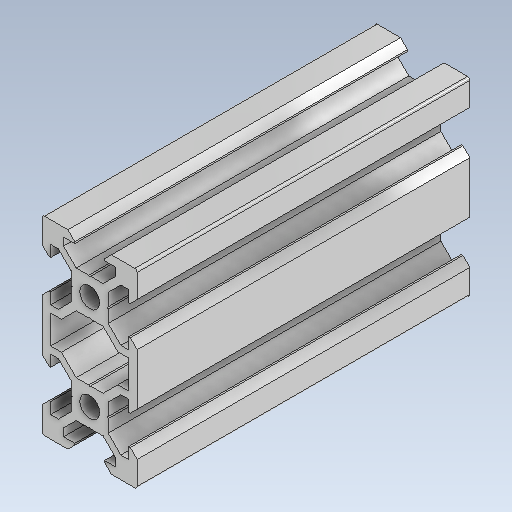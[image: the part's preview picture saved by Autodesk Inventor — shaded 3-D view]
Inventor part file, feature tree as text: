
AUTODESK INVENTOR PART (.ipt)
format: ipt  version: 2020 (Build 240168000, 168)  size: 277,504 bytes
history: native  units: mm
features: extrude x1, sketch x1
ambient origin geometry x8: Origin, YZ Plane, XZ Plane, XY Plane, X Axis, Y Axis, Z Axis, Center Point
bodies: Solid1 (feature_tree)
feature tree (2):
  extrude  "Extrusion1"  [1 undecoded]
  sketch  "Sketch1"  dims[d0=70.0mm d1=0.0mm]
note: 1 required parameter value undecoded (feature->parameter linkage not recoverable at this tier; creation-order binding heuristic only, values carry confidence <= 0.55)
